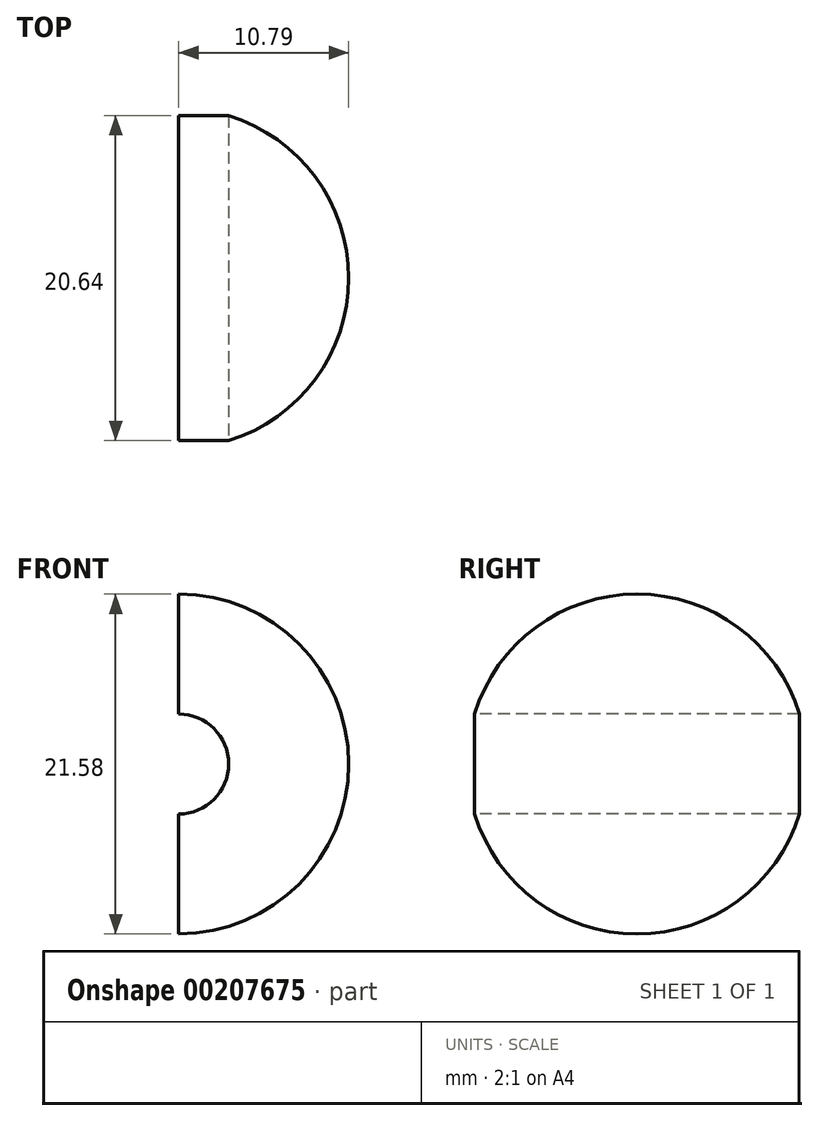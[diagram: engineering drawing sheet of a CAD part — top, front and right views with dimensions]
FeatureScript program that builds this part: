
annotation { "Feature Type Name" : "Feature", "Feature Type Description" : "" }
export const myFeature = defineFeature(function(context is Context, id is Id, definition is map)
    precondition{}
    {
        {
            var Q0;
            Q0=qCreatedBy(makeId("Front.planeOp"),FACE);
            var sketch = newSketch(context, id + "F0", { "sketchPlane" : qUnion([Q0])});
            skArc(sketch, "E0", {"start": v(0, -10.8) * mm, "mid": v(10.8, 0) * mm, "end": v(0, 10.8) * mm});
            skLineSegment(sketch, "E1", {"start": v(0, 10.8) * mm, "end": v(0, -10.8) * mm});
            skSolve(sketch);
        }
        {
            var Q0;
            Q0=makeQuery(id+"F0.imprint","IMPRINT",FACE,{"disambiguationData":[TD([[makeQuery(id+"F0.imprint","IMPRINT",EDGE,{"derivedFrom":sQuery(id+"F0.wireOp",EDGE,"E0")}),1.0]])]});
            var Q1;
            Q1=sQuery(id+"F0.wireOp",EDGE,"E1");
            revolve(context, id + "F1", {"entities" : qUnion([Q0]), "axis" : qUnion([Q1]), "revolveType" : RevolveType.FULL});
        }
        {
            var Q0;
            Q0=makeQuery(id+"F1.opRevolve","SWEPT_BODY",BODY,{"disambiguationData":[OSD([sQuery(id+"F0.wireOp",EDGE,"E0"),sQuery(id+"F0.wireOp",EDGE,"E1")])]});
            transform(context, id + "F2", {"entities" : qUnion([Q0]), "transformType" : TransformType.TRANSLATION_3D, "dx" : 0 * mm, "dy" : 0 * mm, "dz" : 0 * mm, "makeCopy" : true});
        }
        {
            var Q0;
            Q0=qCreatedBy(makeId("Front.planeOp"),FACE);
            var sketch = newSketch(context, id + "F3", { "sketchPlane" : qUnion([Q0])});
            skArc(sketch, "E2", {"start": v(0, 9.53) * mm, "mid": v(-6.74, 6.74) * mm, "end": v(-9.53, 0) * mm});
            skLineSegment(sketch, "E3", {"start": v(0, 9.27) * mm, "end": v(0, -9.53) * mm});
            skLineSegment(sketch, "E4", {"start": v(0, 0) * mm, "end": v(-9.53, 0) * mm});
            skPoint(sketch, "E5.orphan", {"position": v(0, 9.53) * mm});
            skLineSegment(sketch, "E6", {"start": v(0, 9.27) * mm, "end": v(0, 9.53) * mm});
            skLineSegment(sketch, "E7", {"start": v(-9.53, 0) * mm, "end": v(-11.87, 0) * mm});
            skLineSegment(sketch, "E8", {"start": v(0, 9.53) * mm, "end": v(0, 11.94) * mm});
            skArc(sketch, "E9", {"start": v(0, 11.94) * mm, "mid": v(-8.64, 8.66) * mm, "end": v(-11.87, 0) * mm});
            skSolve(sketch);
        }
        {
            var Q0;
            Q0 = qSketchRegion(id + "F3", true);
            var Q1;
            Q1=sQuery(id+"F3.wireOp",EDGE,"E4");
            revolve(context, id + "F4", {"operationType" : NewBodyOperationType.REMOVE, "entities" : qUnion([Q0]), "axis" : qUnion([Q1]), "revolveType" : RevolveType.FULL, "oppositeDirection" : true});
        }
        {
            var Q0;
            Q0=qCreatedBy(makeId("Front.planeOp"),FACE);
            var sketch = newSketch(context, id + "F5", { "sketchPlane" : qUnion([Q0])});
            skCircle(sketch, "E10", {"center": v(0, 0) * mm, "radius": 3.18 * mm});
            skSolve(sketch);
        }
        {
            var Q0;
            Q0 = qSketchRegion(id + "F5", true);
            extrude(context, id + "F6", {"entities" : qUnion([Q0]), "operationType" : NewBodyOperationType.REMOVE, "endBound" : BoundingType.THROUGH_ALL, "oppositeDirection" : true, "depth" : 25.4 * mm, "hasSecondDirection" : true, "secondDirectionBound" : SecondDirectionBoundingType.THROUGH_ALL, "secondDirectionOppositeDirection" : false, "secondDirectionDepth" : 25.4 * mm});
        }
    });
